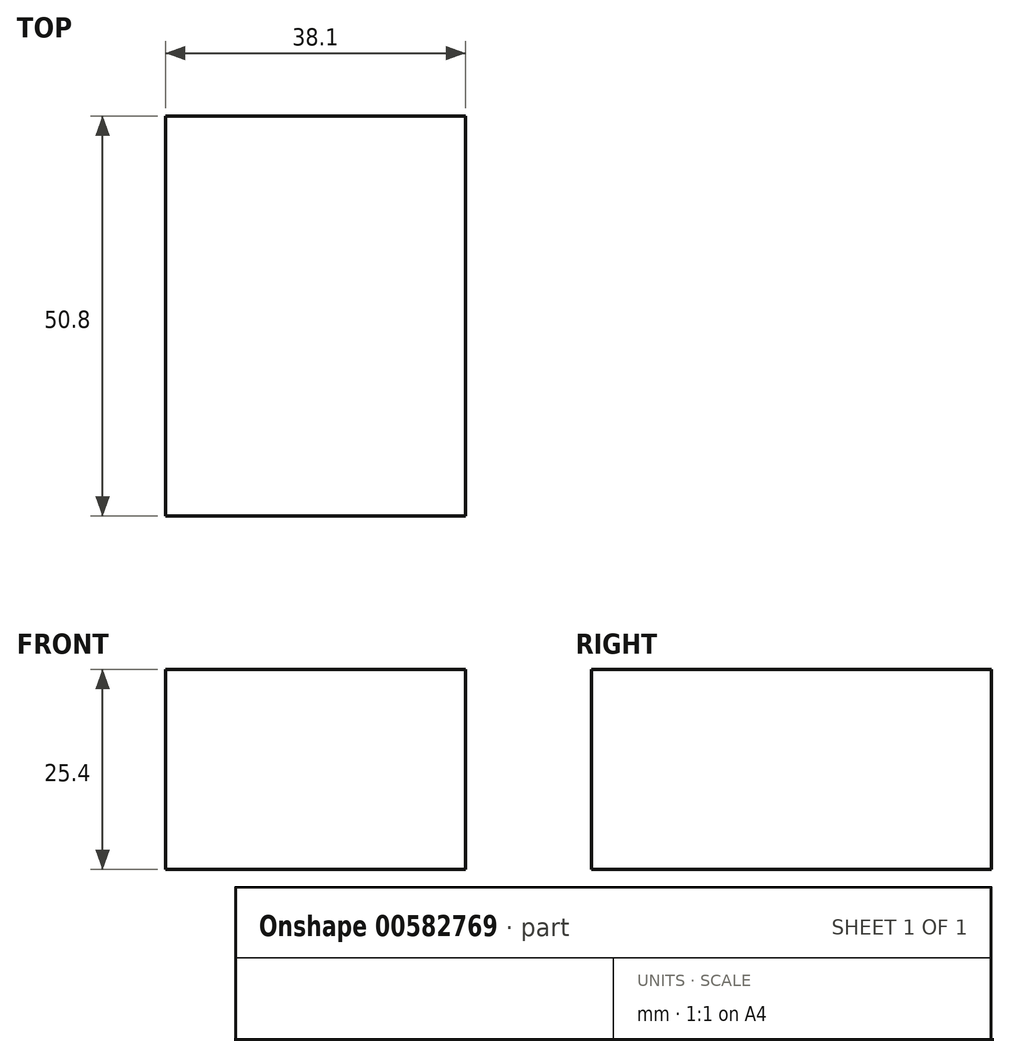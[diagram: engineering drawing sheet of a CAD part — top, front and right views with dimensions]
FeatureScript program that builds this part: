
annotation { "Feature Type Name" : "Feature", "Feature Type Description" : "" }
export const myFeature = defineFeature(function(context is Context, id is Id, definition is map)
    precondition{}
    {
        {
            var Q0;
            Q0=qCreatedBy(makeId("Top.planeOp"),FACE);
            var sketch = newSketch(context, id + "F0", { "sketchPlane" : qUnion([Q0])});
            skLineSegment(sketch, "E0.bottom", {"start": v(0, 0) * mm, "end": v(38.1, 0) * mm});
            skLineSegment(sketch, "E0.top", {"start": v(0, 50.8) * mm, "end": v(38.1, 50.8) * mm});
            skLineSegment(sketch, "E0.left", {"start": v(0, 0) * mm, "end": v(0, 50.8) * mm});
            skLineSegment(sketch, "E0.right", {"start": v(38.1, 0) * mm, "end": v(38.1, 50.8) * mm});
            skSolve(sketch);
        }
        {
            var Q0;
            Q0 = qSketchRegion(id + "F0", true);
            extrude(context, id + "F1", {"entities" : qUnion([Q0]), "depth" : 25.4 * mm, "offsetDistance" : 25.4 * mm});
        }
    });
